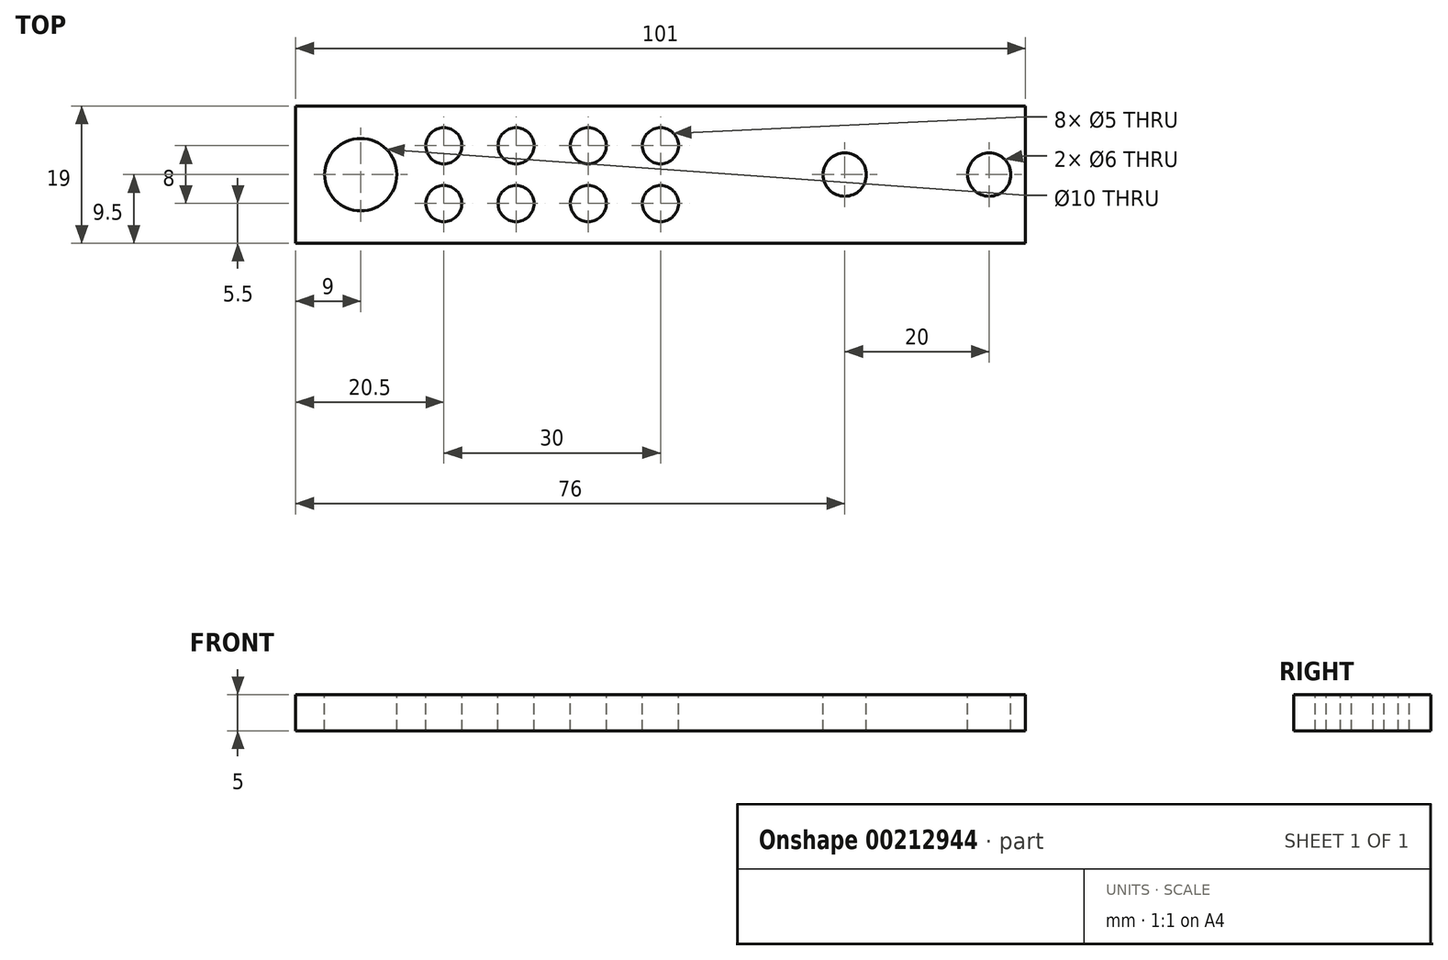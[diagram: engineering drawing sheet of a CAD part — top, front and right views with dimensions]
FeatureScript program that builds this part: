
annotation { "Feature Type Name" : "Feature", "Feature Type Description" : "" }
export const myFeature = defineFeature(function(context is Context, id is Id, definition is map)
    precondition{}
    {
        {
            var Q0;
            Q0=qCreatedBy(makeId("Top.planeOp"),FACE);
            var sketch = newSketch(context, id + "F0", { "sketchPlane" : qUnion([Q0])});
            skLineSegment(sketch, "E0.bottom", {"start": v(-50.5, 9.5) * mm, "end": v(50.5, 9.5) * mm});
            skLineSegment(sketch, "E0.top", {"start": v(-50.5, -9.5) * mm, "end": v(50.5, -9.5) * mm});
            skLineSegment(sketch, "E0.left", {"start": v(-50.5, 9.5) * mm, "end": v(-50.5, -9.5) * mm});
            skLineSegment(sketch, "E0.right", {"start": v(50.5, 9.5) * mm, "end": v(50.5, -9.5) * mm});
            skSolve(sketch);
        }
        {
            var Q0;
            Q0 = qSketchRegion(id + "F0", true);
            extrude(context, id + "F1", {"entities" : qUnion([Q0]), "depth" : 5 * mm});
        }
        {
            var Q0;
            Q0=makeQuery(id+"F1.opExtrude","CAP_FACE",FACE,{"disambiguationData":[OSD([sQuery(id+"F0.wireOp",EDGE,"E0.bottom"),sQuery(id+"F0.wireOp",EDGE,"E0.top"),sQuery(id+"F0.wireOp",EDGE,"E0.left"),sQuery(id+"F0.wireOp",EDGE,"E0.right")])],"isStart":false});
            var sketch = newSketch(context, id + "F2", { "sketchPlane" : qUnion([Q0])});
            skPoint(sketch, "E1", {"position": v(25.5, 0) * mm});
            skPoint(sketch, "E2", {"position": v(45.5, 0) * mm});
            skSolve(sketch);
        }
        {
            var Q0;
            Q0=sQuery(id+"F2.wireOp",VERTEX,"E1");
            var Q1;
            Q1=sQuery(id+"F2.wireOp",VERTEX,"E2");
            var Q2;
            Q2=makeQuery(id+"F1.opExtrude","SWEPT_BODY",BODY,{"disambiguationData":[OSD([sQuery(id+"F0.wireOp",EDGE,"E0.bottom"),sQuery(id+"F0.wireOp",EDGE,"E0.top"),sQuery(id+"F0.wireOp",EDGE,"E0.left"),sQuery(id+"F0.wireOp",EDGE,"E0.right")])]});
            hole(context, id + "F3", {"style" : HoleStyle.SIMPLE, "endStyle" : HoleEndStyle.THROUGH, "holeDiameter" : 6 * mm, "locations" : qUnion([Q0, Q1]), "scope" : qUnion([Q2]), "isTappedThrough" : true});
        }
        {
            var Q0;
            Q0=makeQuery(id+"F1.opExtrude","CAP_FACE",FACE,{"disambiguationData":[OSD([sQuery(id+"F0.wireOp",EDGE,"E0.bottom"),sQuery(id+"F0.wireOp",EDGE,"E0.top"),sQuery(id+"F0.wireOp",EDGE,"E0.left"),sQuery(id+"F0.wireOp",EDGE,"E0.right")])],"isStart":false});
            var sketch = newSketch(context, id + "F4", { "sketchPlane" : qUnion([Q0])});
            skPoint(sketch, "E3", {"position": v(-41.5, 0) * mm});
            skPoint(sketch, "E3.positionSnap0", {"position": v(-50.5, 0) * mm});
            skSolve(sketch);
        }
        {
            var Q0;
            Q0=sQuery(id+"F4.wireOp",VERTEX,"E3");
            var Q1;
            Q1=makeQuery(id+"F1.opExtrude","SWEPT_BODY",BODY,{"disambiguationData":[OSD([sQuery(id+"F0.wireOp",EDGE,"E0.bottom"),sQuery(id+"F0.wireOp",EDGE,"E0.top"),sQuery(id+"F0.wireOp",EDGE,"E0.left"),sQuery(id+"F0.wireOp",EDGE,"E0.right")])]});
            hole(context, id + "F5", {"style" : HoleStyle.SIMPLE, "endStyle" : HoleEndStyle.THROUGH, "holeDiameter" : 10 * mm, "locations" : qUnion([Q0]), "scope" : qUnion([Q1]), "isTappedThrough" : true});
        }
        {
            var Q0;
            Q0=makeQuery(id+"F1.opExtrude","CAP_FACE",FACE,{"disambiguationData":[OSD([sQuery(id+"F0.wireOp",EDGE,"E0.bottom"),sQuery(id+"F0.wireOp",EDGE,"E0.top"),sQuery(id+"F0.wireOp",EDGE,"E0.left"),sQuery(id+"F0.wireOp",EDGE,"E0.right")])],"isStart":false});
            var sketch = newSketch(context, id + "F6", { "sketchPlane" : qUnion([Q0])});
            skPoint(sketch, "E4", {"position": v(-30, 4) * mm});
            skPoint(sketch, "E5", {"position": v(-20, 4) * mm});
            skPoint(sketch, "E6", {"position": v(-10, 4) * mm});
            skPoint(sketch, "E7", {"position": v(0, 4) * mm});
            skPoint(sketch, "E8", {"position": v(-30, -4) * mm});
            skPoint(sketch, "E9", {"position": v(-20, -4) * mm});
            skPoint(sketch, "E10", {"position": v(-10, -4) * mm});
            skPoint(sketch, "E11", {"position": v(0, -4) * mm});
            skSolve(sketch);
        }
        {
            var Q0;
            Q0=sQuery(id+"F6.wireOp",VERTEX,"E4");
            var Q1;
            Q1=sQuery(id+"F6.wireOp",VERTEX,"E5");
            var Q2;
            Q2=sQuery(id+"F6.wireOp",VERTEX,"E6");
            var Q3;
            Q3=sQuery(id+"F6.wireOp",VERTEX,"E7");
            var Q4;
            Q4=sQuery(id+"F6.wireOp",VERTEX,"E11");
            var Q5;
            Q5=sQuery(id+"F6.wireOp",VERTEX,"E10");
            var Q6;
            Q6=sQuery(id+"F6.wireOp",VERTEX,"E9");
            var Q7;
            Q7=sQuery(id+"F6.wireOp",VERTEX,"E8");
            var Q8;
            Q8=makeQuery(id+"F1.opExtrude","SWEPT_BODY",BODY,{"disambiguationData":[OSD([sQuery(id+"F0.wireOp",EDGE,"E0.bottom"),sQuery(id+"F0.wireOp",EDGE,"E0.top"),sQuery(id+"F0.wireOp",EDGE,"E0.left"),sQuery(id+"F0.wireOp",EDGE,"E0.right")])]});
            hole(context, id + "F7", {"style" : HoleStyle.SIMPLE, "endStyle" : HoleEndStyle.THROUGH, "holeDiameter" : 5 * mm, "locations" : qUnion([Q0, Q1, Q2, Q3, Q4, Q5, Q6, Q7]), "scope" : qUnion([Q8]), "isTappedThrough" : true});
        }
    });
